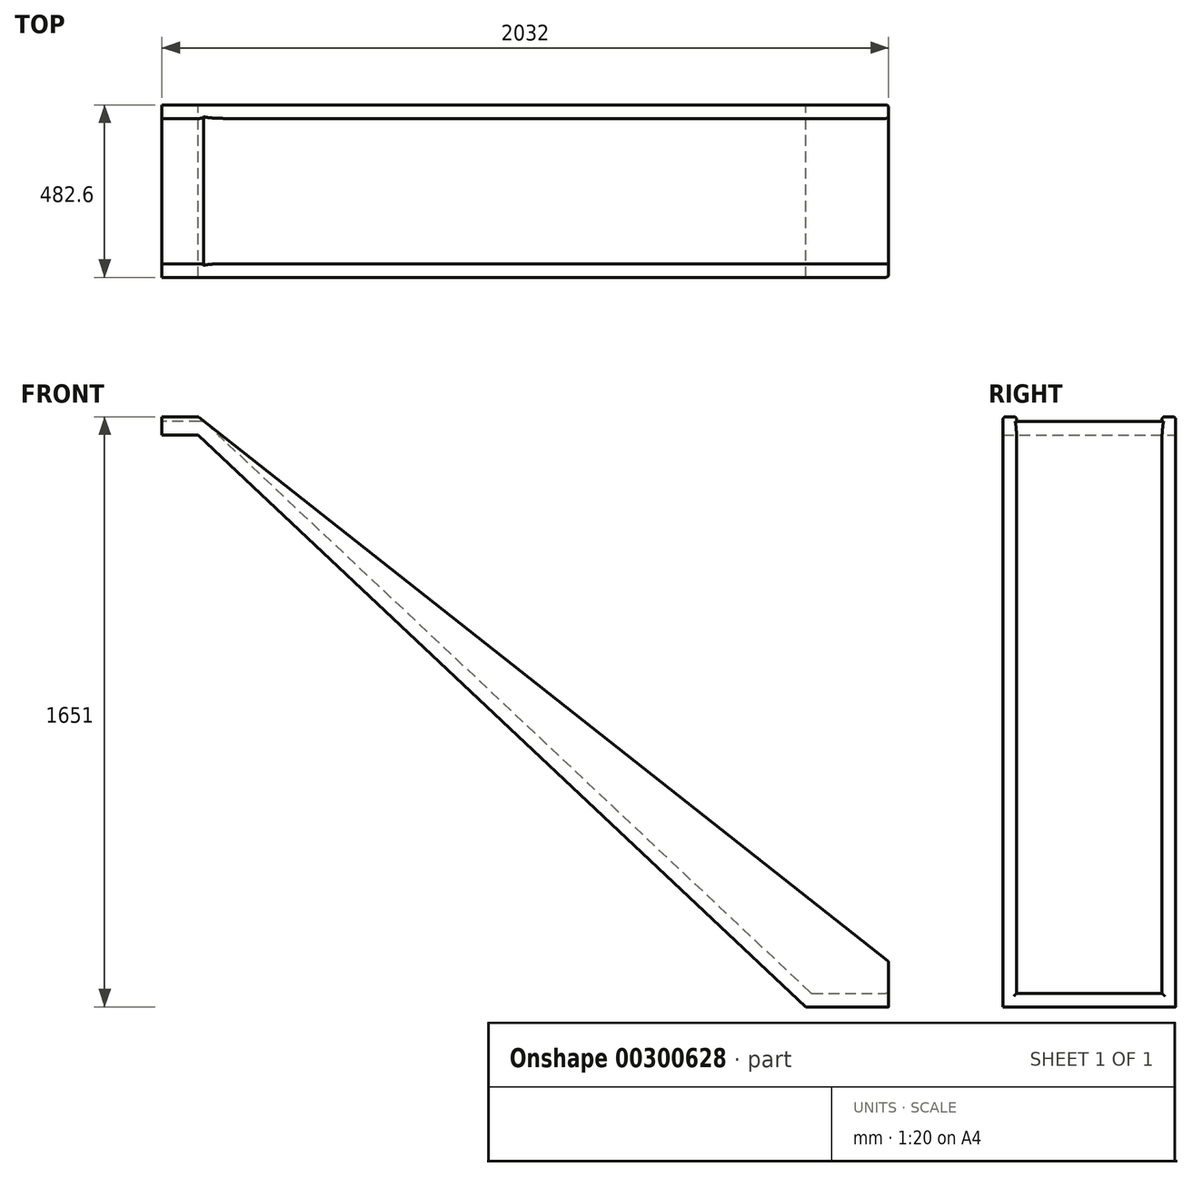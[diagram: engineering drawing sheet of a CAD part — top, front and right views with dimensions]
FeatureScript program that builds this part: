
annotation { "Feature Type Name" : "Feature", "Feature Type Description" : "" }
export const myFeature = defineFeature(function(context is Context, id is Id, definition is map)
    precondition{}
    {
        {
            var Q0;
            Q0=qCreatedBy(makeId("Front.planeOp"),FACE);
            var sketch = newSketch(context, id + "F0", { "sketchPlane" : qUnion([Q0])});
            skLineSegment(sketch, "E0", {"start": v(0, 0) * mm, "end": v(231.72, 0) * mm});
            skLineSegment(sketch, "E1", {"start": v(231.72, 0) * mm, "end": v(231.72, 127) * mm});
            skLineSegment(sketch, "E2", {"start": v(0, 0) * mm, "end": v(-1698.68, 1600.2) * mm});
            skLineSegment(sketch, "E3", {"start": v(-1698.68, 1600.2) * mm, "end": v(-1800.28, 1600.2) * mm});
            skLineSegment(sketch, "E4", {"start": v(-1800.28, 1600.2) * mm, "end": v(-1800.28, 1651) * mm});
            skLineSegment(sketch, "E5", {"start": v(-1800.28, 1651) * mm, "end": v(-1698.68, 1651) * mm});
            skLineSegment(sketch, "E6", {"start": v(-1698.68, 1651) * mm, "end": v(231.72, 127) * mm});
            skSolve(sketch);
        }
        {
            var Q0;
            Q0 = qSketchRegion(id + "F0", true);
            extrude(context, id + "F1", {"entities" : qUnion([Q0]), "depth" : 482.6 * mm});
        }
        {
            var Q0;
            Q0=makeQuery(id+"F1.opExtrude","SWEPT_FACE",FACE,{"disambiguationData":[OSD([sQuery(id+"F0.wireOp",EDGE,"E6")])]});
            var Q1;
            Q1=makeQuery(id+"F1.opExtrude","SWEPT_FACE",FACE,{"disambiguationData":[OSD([sQuery(id+"F0.wireOp",EDGE,"E1")])]});
            var Q2;
            Q2=makeQuery(id+"F1.opExtrude","SWEPT_FACE",FACE,{"disambiguationData":[OSD([sQuery(id+"F0.wireOp",EDGE,"E5")])]});
            var Q3;
            Q3=makeQuery(id+"F1.opExtrude","SWEPT_FACE",FACE,{"disambiguationData":[OSD([sQuery(id+"F0.wireOp",EDGE,"E4")])]});
            shell(context, id + "F2", {"entities" : qUnion([Q0, Q1, Q2, Q3]), "thickness" : 38.1 * mm});
        }
        {
            var Q0;
            {var subQ0=sQuery(id+"F0.wireOp",EDGE,"E5");Q0=makeQuery(id+"F2.opShell","OFFSET_EDGE",EDGE,{"disambiguationData":[OSD([subQ0]),TDD([makeQuery(id+"F1.opExtrude","CAP_EDGE",EDGE,{"disambiguationData":[OSD([subQ0])],"isStart":false})])]});}
            var Q1;
            {var subQ0=sQuery(id+"F0.wireOp",EDGE,"E6");Q1=makeQuery(id+"F2.opShell","OFFSET_EDGE",EDGE,{"disambiguationData":[OSD([subQ0]),TDD([makeQuery(id+"F1.opExtrude","CAP_EDGE",EDGE,{"disambiguationData":[OSD([subQ0])],"isStart":false})])]});}
            var Q2;
            Q2=makeQuery(id+"F1.opExtrude","CAP_EDGE",EDGE,{"disambiguationData":[OSD([sQuery(id+"F0.wireOp",EDGE,"E5")])],"isStart":false});
            var Q3;
            Q3=makeQuery(id+"F1.opExtrude","CAP_EDGE",EDGE,{"disambiguationData":[OSD([sQuery(id+"F0.wireOp",EDGE,"E6")])],"isStart":false});
            var Q4;
            {var subQ0=sQuery(id+"F0.wireOp",EDGE,"E5");Q4=makeQuery(id+"F2.opShell","OFFSET_EDGE",EDGE,{"disambiguationData":[OSD([subQ0]),TDD([makeQuery(id+"F1.opExtrude","CAP_EDGE",EDGE,{"disambiguationData":[OSD([subQ0])],"isStart":true})])]});}
            var Q5;
            Q5=makeQuery(id+"F1.opExtrude","CAP_EDGE",EDGE,{"disambiguationData":[OSD([sQuery(id+"F0.wireOp",EDGE,"E5")])],"isStart":true});
            var Q6;
            Q6=makeQuery(id+"F1.opExtrude","CAP_EDGE",EDGE,{"disambiguationData":[OSD([sQuery(id+"F0.wireOp",EDGE,"E6")])],"isStart":true});
            var Q7;
            {var subQ0=sQuery(id+"F0.wireOp",EDGE,"E6");Q7=makeQuery(id+"F2.opShell","OFFSET_EDGE",EDGE,{"disambiguationData":[OSD([subQ0]),TDD([makeQuery(id+"F1.opExtrude","CAP_EDGE",EDGE,{"disambiguationData":[OSD([subQ0])],"isStart":true})])]});}
            var Q8;
            Q8=makeQuery(id+"F2.opShell","OFFSET_EDGE",EDGE,{"disambiguationData":[OSD([sQuery(id+"F0.wireOp",EDGE,"E5"),sQuery(id+"F0.wireOp",EDGE,"E6")])]});
            var Q9;
            Q9=makeQuery(id+"F1.opExtrude","SWEPT_EDGE",EDGE,{"disambiguationData":[OSD([sQuery(id+"F0.wireOp",EDGE,"E5"),sQuery(id+"F0.wireOp",EDGE,"E6")])]});
            var Q10;
            Q10=makeQuery(id+"F1.opExtrude","SWEPT_EDGE",EDGE,{"disambiguationData":[OSD([sQuery(id+"F0.wireOp",EDGE,"E1"),sQuery(id+"F0.wireOp",EDGE,"E6")])]});
            var Q11;
            Q11=makeQuery(id+"F1.opExtrude","CAP_EDGE",EDGE,{"disambiguationData":[OSD([sQuery(id+"F0.wireOp",EDGE,"E1")])],"isStart":false});
            var Q12;
            Q12=makeQuery(id+"F2.opShell","OFFSET_EDGE",EDGE,{"disambiguationData":[OSD([sQuery(id+"F0.wireOp",EDGE,"E1"),sQuery(id+"F0.wireOp",EDGE,"E6")])]});
            var Q13;
            Q13=makeQuery(id+"F1.opExtrude","CAP_EDGE",EDGE,{"disambiguationData":[OSD([sQuery(id+"F0.wireOp",EDGE,"E1")])],"isStart":true});
            var Q14;
            {var subQ0=sQuery(id+"F0.wireOp",EDGE,"E1");Q14=makeQuery(id+"F2.opShell","OFFSET_EDGE",EDGE,{"disambiguationData":[OSD([subQ0]),TDD([makeQuery(id+"F1.opExtrude","CAP_EDGE",EDGE,{"disambiguationData":[OSD([subQ0])],"isStart":true})])]});}
            var Q15;
            {var subQ0=sQuery(id+"F0.wireOp",EDGE,"E1");Q15=makeQuery(id+"F2.opShell","OFFSET_EDGE",EDGE,{"disambiguationData":[OSD([subQ0]),TDD([makeQuery(id+"F1.opExtrude","CAP_EDGE",EDGE,{"disambiguationData":[OSD([subQ0])],"isStart":false})])]});}
            var Q16;
            Q16=makeQuery(id+"F2.opShell","OFFSET_EDGE",EDGE,{"disambiguationData":[OSD([sQuery(id+"F0.wireOp",EDGE,"E0"),sQuery(id+"F0.wireOp",EDGE,"E1")])]});
            var Q17;
            Q17=makeQuery(id+"F2.opShell","OFFSET_EDGE",EDGE,{"disambiguationData":[OSD([sQuery(id+"F0.wireOp",EDGE,"E0"),sQuery(id+"F0.wireOp",EDGE,"E2")])]});
            fillet(context, id + "F3", {"entities" : qUnion([Q0, Q1, Q2, Q3, Q4, Q5, Q6, Q7, Q8, Q9, Q10, Q11, Q12, Q13, Q14, Q15, Q16, Q17]), "radius" : 7.62 * mm, "tangentPropagation" : true, "allowEdgeOverflow" : false});
        }
    });
